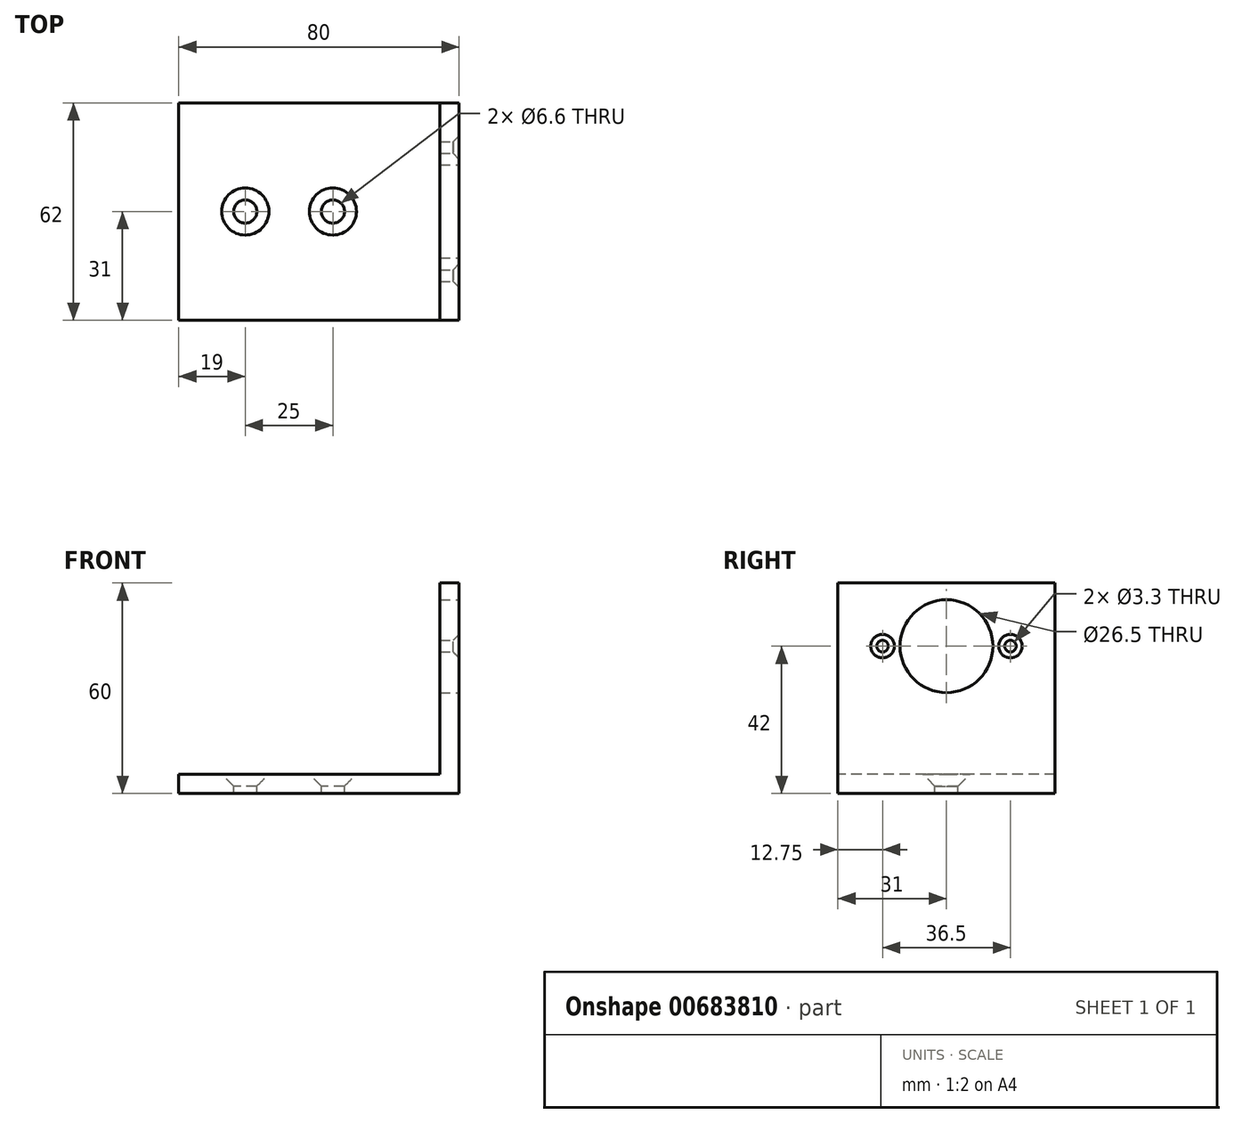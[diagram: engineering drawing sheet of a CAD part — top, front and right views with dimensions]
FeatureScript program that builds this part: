
annotation { "Feature Type Name" : "Feature", "Feature Type Description" : "" }
export const myFeature = defineFeature(function(context is Context, id is Id, definition is map)
    precondition{}
    {
        {
            var Q0;
            Q0=qCreatedBy(makeId("Front.planeOp"),FACE);
            var sketch = newSketch(context, id + "F0", { "sketchPlane" : qUnion([Q0])});
            skLineSegment(sketch, "E0", {"start": v(0, 0) * mm, "end": v(80, 0) * mm});
            skLineSegment(sketch, "E1", {"start": v(80, 0) * mm, "end": v(80, 60) * mm});
            skLineSegment(sketch, "E2.0", {"start": v(74.5, 5.5) * mm, "end": v(74.5, 60) * mm});
            skLineSegment(sketch, "E3.0", {"start": v(0, 5.5) * mm, "end": v(74.5, 5.5) * mm});
            skLineSegment(sketch, "E4", {"start": v(74.5, 60) * mm, "end": v(80, 60) * mm});
            skLineSegment(sketch, "E5", {"start": v(0, 5.5) * mm, "end": v(0, 0) * mm});
            skSolve(sketch);
        }
        {
            var Q0;
            Q0=makeQuery(id+"F0.imprint","IMPRINT",FACE,{"disambiguationData":[TD([[makeQuery(id+"F0.imprint","IMPRINT",EDGE,{"derivedFrom":sQuery(id+"F0.wireOp",EDGE,"E0")}),1.0]])]});
            extrude(context, id + "F1", {"entities" : qUnion([Q0]), "oppositeDirection" : true, "depth" : 62 * mm, "offsetDistance" : 25 * mm});
        }
        {
            var Q0;
            Q0=makeQuery(id+"F1.opExtrude","SWEPT_FACE",FACE,{"disambiguationData":[OSD([sQuery(id+"F0.wireOp",EDGE,"E1")])]});
            var sketch = newSketch(context, id + "F2", { "sketchPlane" : qUnion([Q0])});
            skLineSegment(sketch, "E6", {"start": v(31, 60) * mm, "end": v(31, 42) * mm, "construction": true});
            skSolve(sketch);
        }
        {
            var Q0;
            Q0=sQuery(id+"F2.wireOp",VERTEX,"E6.end");
            var Q1;
            Q1=makeQuery(id+"F1.opExtrude","SWEPT_BODY",BODY,{"disambiguationData":[OSD([sQuery(id+"F0.wireOp",EDGE,"E0"),sQuery(id+"F0.wireOp",EDGE,"E1"),sQuery(id+"F0.wireOp",EDGE,"E2.0"),sQuery(id+"F0.wireOp",EDGE,"E3.0"),sQuery(id+"F0.wireOp",EDGE,"E4"),sQuery(id+"F0.wireOp",EDGE,"E5")])]});
            hole(context, id + "F3", {"style" : HoleStyle.SIMPLE, "endStyle" : HoleEndStyle.THROUGH, "holeDiameter" : 26.5 * mm, "majorDiameter" : 5 * mm, "isTappedThrough" : true, "tappedDepth" : 12 * mm, "tapClearance" : 3, "startFromSketch" : true, "locations" : qUnion([Q0]), "scope" : qUnion([Q1])});
        }
        {
            var Q0;
            {var subQ0=sQuery(id+"F0.wireOp",EDGE,"E1");Q0=makeQuery(id+"F2.imprint","IMPRINT",FACE,{"disambiguationData":[TD([[makeQuery(id+"F2.imprint","IMPRINT",EDGE,{"derivedFrom":makeQuery(id+"F1.opExtrude","CAP_EDGE",EDGE,{"disambiguationData":[OSD([subQ0])],"isStart":true})}),-1.0]])]});}
            var sketch = newSketch(context, id + "F4", { "sketchPlane" : qUnion([Q0])});
            skLineSegment(sketch, "E7", {"start": v(49.25, 42) * mm, "end": v(12.75, 42) * mm, "construction": true});
            skSolve(sketch);
        }
        {
            var Q0;
            Q0=sQuery(id+"F4.wireOp",VERTEX,"E7.end");
            var Q1;
            Q1=sQuery(id+"F4.wireOp",VERTEX,"E7.start");
            var Q2;
            Q2=makeQuery(id+"F1.opExtrude","SWEPT_BODY",BODY,{"disambiguationData":[OSD([sQuery(id+"F0.wireOp",EDGE,"E0"),sQuery(id+"F0.wireOp",EDGE,"E1"),sQuery(id+"F0.wireOp",EDGE,"E2.0"),sQuery(id+"F0.wireOp",EDGE,"E3.0"),sQuery(id+"F0.wireOp",EDGE,"E4"),sQuery(id+"F0.wireOp",EDGE,"E5")])]});
            hole(context, id + "F5", {"style" : HoleStyle.C_SINK, "endStyle" : HoleEndStyle.THROUGH, "standardTappedOrClearance" : lookupTablePath({ "standard" : "ISO", "fit" : "Normal", "size" : "M3", "type" : "Clearance" }), "standardBlindInLast" : lookupTablePath({ "fit" : "Standard", "standard" : "ISO", "size" : "M3", "type" : "Clearance" }), "holeDiameter" : 3.3 * mm, "cSinkDiameter" : 6.72 * mm, "cSinkAngle" : 90 * degree, "majorDiameter" : 5 * mm, "isTappedThrough" : true, "tappedDepth" : 12 * mm, "tapClearance" : 3, "startFromSketch" : true, "locations" : qUnion([Q0, Q1]), "scope" : qUnion([Q2])});
        }
        {
            var Q0;
            Q0=makeQuery(id+"F1.opExtrude","SWEPT_FACE",FACE,{"disambiguationData":[OSD([sQuery(id+"F0.wireOp",EDGE,"E3.0")])]});
            var sketch = newSketch(context, id + "F6", { "sketchPlane" : qUnion([Q0])});
            skLineSegment(sketch, "E8", {"start": v(0, 31) * mm, "end": v(19, 31) * mm, "construction": true});
            skLineSegment(sketch, "E9", {"start": v(19, 31) * mm, "end": v(44, 31) * mm, "construction": true});
            skSolve(sketch);
        }
        {
            var Q0;
            Q0=sQuery(id+"F6.wireOp",VERTEX,"E9.start");
            var Q1;
            Q1=sQuery(id+"F6.wireOp",VERTEX,"E9.end");
            var Q2;
            Q2=makeQuery(id+"F1.opExtrude","SWEPT_BODY",BODY,{"disambiguationData":[OSD([sQuery(id+"F0.wireOp",EDGE,"E0"),sQuery(id+"F0.wireOp",EDGE,"E1"),sQuery(id+"F0.wireOp",EDGE,"E2.0"),sQuery(id+"F0.wireOp",EDGE,"E3.0"),sQuery(id+"F0.wireOp",EDGE,"E4"),sQuery(id+"F0.wireOp",EDGE,"E5")])]});
            hole(context, id + "F7", {"style" : HoleStyle.C_SINK, "endStyle" : HoleEndStyle.THROUGH, "standardTappedOrClearance" : lookupTablePath({ "standard" : "ISO", "fit" : "Normal", "size" : "M6", "type" : "Clearance" }), "standardBlindInLast" : lookupTablePath({ "fit" : "Standard", "standard" : "ISO", "size" : "M6", "type" : "Clearance" }), "holeDiameter" : 6.6 * mm, "cSinkDiameter" : 13.44 * mm, "cSinkAngle" : 90 * degree, "majorDiameter" : 5 * mm, "isTappedThrough" : true, "tappedDepth" : 12 * mm, "tapClearance" : 3, "startFromSketch" : true, "locations" : qUnion([Q0, Q1]), "scope" : qUnion([Q2])});
        }
    });
